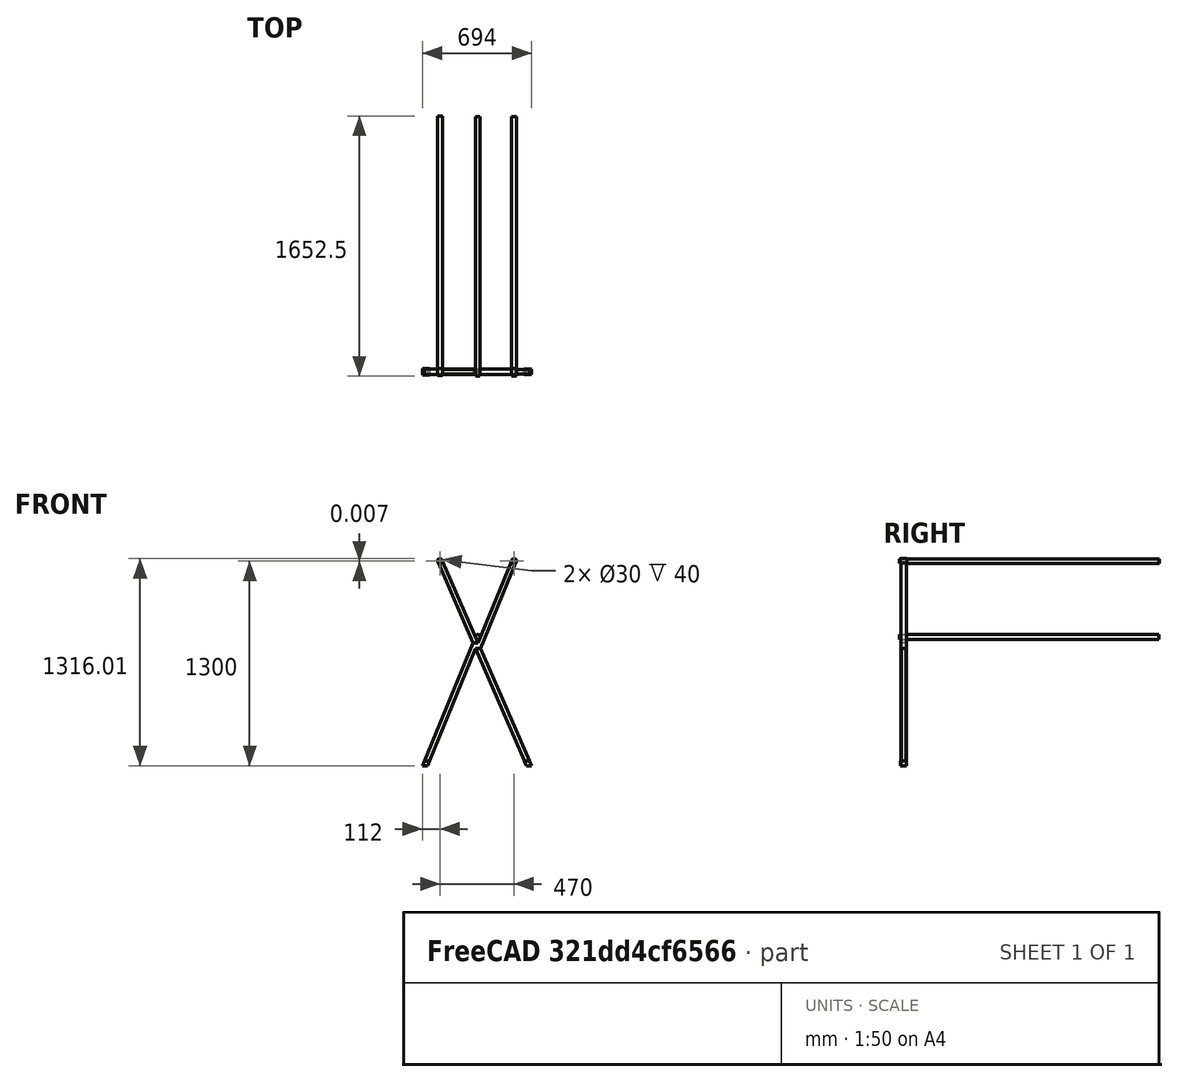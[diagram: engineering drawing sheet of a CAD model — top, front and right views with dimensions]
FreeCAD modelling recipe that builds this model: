
FCSTD DOCUMENT  (FreeCAD 1.0R39109 (Git))
Label: clothesdryingpole
License: All rights reserved
LicenseURL: https://en.wikipedia.org/wiki/All_rights_reserved
objects: Sketcher::SketchObject×9, PartDesign::Pad×8, PartDesign::ShapeBinder×5, PartDesign::Body×4, PartDesign::Line×2, App::Part×2, PartDesign::Pocket×1, Part::FeaturePython×1, Assembly::JointGroup×1, App::Link×1, Assembly::AssemblyObject×1
note: 56 computed .brp shape members not serialized (recipe doc carries the construction recipe); baked Part::Feature solids carry a one-line shape summary decoded from their .brp

FEATURE [Sketcher::SketchObject] Sketch
  ArcFitTolerance = 1e-06
  AttachmentSupport = -> [XZ_Plane]
  FullyConstrained = true
  MakeInternals = false
  MapMode = 5
  Placement = pos=(0,0,0) rot=(1,0,0;1.5708rad)
  sketch-geometry (16):
    g0: LineSegment StartX=-345 StartY=0 StartZ=0 EndX=-315 EndY=0 EndZ=0
    g1: LineSegment [constr] StartX=315 StartY=0 StartZ=0 EndX=345 EndY=0 EndZ=0
    g2: LineSegment [constr] StartX=-250 StartY=1300 StartZ=0 EndX=-220 EndY=1300 EndZ=0
    g3: LineSegment StartX=220 StartY=1300 StartZ=0 EndX=250 EndY=1300 EndZ=0
    g4: LineSegment [constr] StartX=-220 StartY=1300 StartZ=0 EndX=345 EndY=0 EndZ=0
    g5: LineSegment [constr] StartX=315 StartY=0 StartZ=0 EndX=-250 EndY=1300 EndZ=0
    g6: LineSegment StartX=220 StartY=1300 StartZ=0 EndX=6 EndY=780 EndZ=0
    g7: LineSegment StartX=-345 StartY=0 StartZ=0 EndX=-24 EndY=780 EndZ=0
    g8: LineSegment StartX=-315 StartY=0 StartZ=0 EndX=-8.59091 EndY=744.545 EndZ=0
    g9: LineSegment StartX=250 StartY=1300 StartZ=0 EndX=21.4091 EndY=744.545 EndZ=0
    g10: LineSegment [constr] StartX=-8.59091 StartY=744.545 StartZ=0 EndX=-8.59091 EndY=780 EndZ=0
    g11: LineSegment [constr] StartX=-8.59091 StartY=780 StartZ=0 EndX=-24 EndY=780 EndZ=0
    g12: LineSegment [constr] StartX=6 StartY=780 StartZ=0 EndX=6 EndY=744.545 EndZ=0
    g13: LineSegment [constr] StartX=21.4091 StartY=744.545 StartZ=0 EndX=6 EndY=744.545 EndZ=0
    g14: LineSegment StartX=-24 StartY=780 StartZ=0 EndX=6 EndY=780 EndZ=0
    g15: LineSegment StartX=-8.59091 StartY=744.545 StartZ=0 EndX=21.4091 EndY=744.545 EndZ=0
  constraints (44):
    c: PointOnObject(g0,g-1)
    c: PointOnObject(g0,g-1)
    c: PointOnObject(g1,g-1)
    c: Symmetric(g1,g0,g-1)
    c: DistanceX(g0,g1) = 690
    c: Equal(g1,g0)
    c: Horizontal(g2)
    c: DistanceY(g-1,g2) = 1300
    c: Symmetric(g3,g2,g-2)
    c: Horizontal(g3)
    c: DistanceX(g2,g3) = 500
    c: Equal(g3,g2)
    c: Equal(g2,g1)
    c: Coincident(g4,g2)
    c: Coincident(g4,g1)
    c: Coincident(g5,g1)
    c: Coincident(g5,g2)
    c: Coincident(g6,g3)
    c: Coincident(g7,g0)
    c: Coincident(g8,g0)
    c: Parallel(g6,g8)
    c: Parallel(g8,g7)
    c: Coincident(g9,g3)
    c: Parallel(g9,g6)
    c: Coincident(g10,g8)
    c: Vertical(g10)
    c: Coincident(g11,g10)
    c: Coincident(g11,g7)
    c: Horizontal(g11)
    c: Coincident(g12,g6)
    c: Vertical(g12)
    c: Coincident(g13,g9)
    c: Coincident(g13,g12)
    c: Horizontal(g13)
    c: Equal(g13,g11)
    c: PointOnObject(g9,g4)
    c: PointOnObject(g7,g5)
    c: PointOnObject(g8,g5)
    c: Horizontal(g6,g7)
    c: DistanceX(g0,g0) = 30
    c: Coincident(g14,g7)
    c: Coincident(g14,g6)
    c: Coincident(g15,g8)
    c: Coincident(g15,g9)
FEATURE [PartDesign::Pad] Pad
  Direction = (0,-1,2e-16)
  Length = 35
  Length2 = 10
  Midplane = true
  Placement = pos=(0,0,0) rot=(1,0,0;1.5708rad)
  Profile = -> Sketch
  ReferenceAxis = -> Sketch [N_Axis]
  Refine = true
  Suppressed = false
  Type = 0
FEATURE [Sketcher::SketchObject] Sketch001
  ArcFitTolerance = 1e-06
  AttachmentSupport = -> [XZ_Plane]
  FullyConstrained = false
  MakeInternals = false
  MapMode = 5
  Placement = pos=(0,0,0) rot=(1,0,0;1.5708rad)
  sketch-geometry (4):
    g0: LineSegment StartX=315 StartY=0 StartZ=0 EndX=345 EndY=0 EndZ=0
    g1: LineSegment StartX=-250 StartY=1300 StartZ=0 EndX=-220 EndY=1300 EndZ=0
    g2: LineSegment StartX=-220 StartY=1300 StartZ=0 EndX=345 EndY=0 EndZ=0
    g3: LineSegment StartX=315 StartY=0 StartZ=0 EndX=-250 EndY=1300 EndZ=0
  constraints (9):
    c: PointOnObject(g0,g-1)
    c: Horizontal(g1)
    c: DistanceY(g-1,g1) = 1300
    c: Equal(g1,g0)
    c: Coincident(g2,g1)
    c: Coincident(g2,g0)
    c: Coincident(g3,g0)
    c: Coincident(g3,g1)
    c: DistanceX(g1,g1) = 30
FEATURE [PartDesign::Pad] Pad001
  BaseFeature = -> Pad
  Direction = (0,-1,2e-16)
  Length = 30
  Length2 = 10
  Midplane = true
  Placement = pos=(0,0,0) rot=(1,0,0;1.5708rad)
  Profile = -> Sketch001
  ReferenceAxis = -> Sketch001 [N_Axis]
  Refine = true
  Suppressed = false
  Type = 0
FEATURE [Sketcher::SketchObject] Sketch002
  ArcFitTolerance = 1e-06
  AttachmentSupport = -> [Pad001]
  ExternalGeometry = -> [Pad001]
  FullyConstrained = true
  MakeInternals = false
  MapMode = 5
  Placement = pos=(0,0,-1e-16) rot=(1,0,0;3.14159rad)
  sketch-geometry (8):
    g0: LineSegment StartX=-347 StartY=19.5 StartZ=0 EndX=-347 EndY=-19.5 EndZ=0
    g1: LineSegment StartX=-347 StartY=-19.5 StartZ=0 EndX=-313 EndY=-19.5 EndZ=0
    g2: LineSegment StartX=-313 StartY=-19.5 StartZ=0 EndX=-313 EndY=19.5 EndZ=0
    g3: LineSegment StartX=-313 StartY=19.5 StartZ=0 EndX=-347 EndY=19.5 EndZ=0
    g4: LineSegment [constr] StartX=-345 StartY=17.5 StartZ=0 EndX=-347 EndY=17.5 EndZ=0
    g5: LineSegment [constr] StartX=-345 StartY=17.5 StartZ=0 EndX=-345 EndY=19.5 EndZ=0
    g6: LineSegment [constr] StartX=-315 StartY=-17.5 StartZ=0 EndX=-315 EndY=-19.5 EndZ=0
    g7: LineSegment [constr] StartX=-315 StartY=-17.5 StartZ=0 EndX=-313 EndY=-17.5 EndZ=0
  constraints (24):
    c: Coincident(g0,g1)
    c: Coincident(g1,g2)
    c: Coincident(g2,g3)
    c: Coincident(g3,g0)
    c: Vertical(g0)
    c: Vertical(g2)
    c: Horizontal(g1)
    c: Horizontal(g3)
    c: Coincident(g4,g-3)
    c: PointOnObject(g4,g0)
    c: Horizontal(g4)
    c: Coincident(g5,g4)
    c: PointOnObject(g5,g3)
    c: Vertical(g5)
    c: Coincident(g6,g-4)
    c: PointOnObject(g6,g1)
    c: Vertical(g6)
    c: Coincident(g7,g6)
    c: PointOnObject(g7,g2)
    c: Horizontal(g7)
    c: Equal(g7,g6)
    c: Equal(g6,g5)
    c: Equal(g5,g4)
    c: DistanceY(g5,g5) = 2
FEATURE [PartDesign::Pad] Pad002
  BaseFeature = -> Pad001
  Direction = (0.380571,2e-16,0.924752)
  Length = 30
  Length2 = 10
  Placement = pos=(0,0,0) rot=(1,0,0;1.5708rad)
  Profile = -> Sketch002
  ReferenceAxis = -> Pad001 [Edge24]
  Refine = true
  Suppressed = false
  Type = 0
FEATURE [Sketcher::SketchObject] Sketch003
  ArcFitTolerance = 1e-06
  AttachmentSupport = -> [Pad002]
  ExternalGeometry = -> [Pad002]
  FullyConstrained = true
  MakeInternals = false
  MapMode = 5
  Placement = pos=(0,0,-1e-16) rot=(1,0,0;3.14159rad)
  sketch-geometry (8):
    g0: LineSegment StartX=313 StartY=17 StartZ=0 EndX=313 EndY=-17 EndZ=0
    g1: LineSegment StartX=313 StartY=-17 StartZ=0 EndX=347 EndY=-17 EndZ=0
    g2: LineSegment StartX=347 StartY=-17 StartZ=0 EndX=347 EndY=17 EndZ=0
    g3: LineSegment StartX=347 StartY=17 StartZ=0 EndX=313 EndY=17 EndZ=0
    g4: LineSegment [constr] StartX=315 StartY=15 StartZ=0 EndX=313 EndY=15 EndZ=0
    g5: LineSegment [constr] StartX=315 StartY=15 StartZ=0 EndX=315 EndY=17 EndZ=0
    g6: LineSegment [constr] StartX=345 StartY=-15 StartZ=0 EndX=345 EndY=-17 EndZ=0
    g7: LineSegment [constr] StartX=345 StartY=-15 StartZ=0 EndX=347 EndY=-15 EndZ=0
  constraints (24):
    c: Coincident(g0,g1)
    c: Coincident(g1,g2)
    c: Coincident(g2,g3)
    c: Coincident(g3,g0)
    c: Vertical(g0)
    c: Vertical(g2)
    c: Horizontal(g1)
    c: Horizontal(g3)
    c: Coincident(g4,g-3)
    c: PointOnObject(g4,g0)
    c: Horizontal(g4)
    c: Coincident(g5,g4)
    c: PointOnObject(g5,g3)
    c: Vertical(g5)
    c: Coincident(g6,g-4)
    c: PointOnObject(g6,g1)
    c: Vertical(g6)
    c: Coincident(g7,g6)
    c: PointOnObject(g7,g2)
    c: Horizontal(g7)
    c: Equal(g5,g4)
    c: Equal(g4,g6)
    c: Equal(g6,g7)
    c: DistanceY(g5,g5) = 2
FEATURE [PartDesign::Pad] Pad003
  BaseFeature = -> Pad002
  Direction = (-0.398597,2e-16,0.917126)
  Length = 30
  Length2 = 10
  Placement = pos=(0,0,0) rot=(1,0,0;1.5708rad)
  Profile = -> Sketch003
  ReferenceAxis = -> Pad002 [Edge49]
  Refine = true
  Suppressed = false
  Type = 0
FEATURE [Sketcher::SketchObject] Sketch004
  ArcFitTolerance = 1e-06
  AttachmentSupport = -> [XZ_Plane]
  ExternalGeometry = -> [Pad003]
  FullyConstrained = true
  MakeInternals = false
  MapMode = 5
  Placement = pos=(0,0,0) rot=(1,0,0;1.5708rad)
  sketch-geometry (4):
    g0: Circle CenterX=-235 CenterY=1300 CenterZ=0 NormalX=0 NormalY=0 NormalZ=1 AngleXU=0 Radius=15
    g1: LineSegment [constr] StartX=-220 StartY=1300 StartZ=0 EndX=-219 EndY=1300 EndZ=0
    g2: Circle CenterX=235 CenterY=1300 CenterZ=0 NormalX=0 NormalY=0 NormalZ=1 AngleXU=0 Radius=15
    g3: LineSegment [constr] StartX=220 StartY=1300 StartZ=0 EndX=219 EndY=1300 EndZ=0
  constraints (14):
    c: PointOnObject(g1,g0)
    c: Horizontal(g1)
    c: DistanceX(g1,g1) = 1
    c: PointOnObject(g-3,g0)
    c: PointOnObject(g-3,g0)
    c: Horizontal(g1,g0)
    c: PointOnObject(g3,g2)
    c: Horizontal(g3,g2)
    c: Horizontal(g3)
    c: Radius(g0) = 15
    c: DistanceX(g3,g3) = 1
    c: Radius(g2) = 15
    c: PointOnObject(g-4,g2)
    c: PointOnObject(g-4,g2)
FEATURE [PartDesign::Pocket] Pocket
  BaseFeature = -> Pad003
  Direction = (0,1,-2e-16)
  Length = 40
  Length2 = 5
  Midplane = true
  Placement = pos=(0,0,0) rot=(1,0,0;1.5708rad)
  Profile = -> Sketch004
  ReferenceAxis = -> Sketch004 [N_Axis]
  Refine = true
  Suppressed = false
  Type = 0
FEATURE [Sketcher::SketchObject] Sketch005
  ArcFitTolerance = 1e-06
  AttachmentSupport = -> [XZ_Plane]
  ExternalGeometry = -> [Pocket]
  FullyConstrained = false
  MakeInternals = false
  MapMode = 5
  Placement = pos=(0,0,0) rot=(1,0,0;1.5708rad)
  sketch-geometry (6):
    g0: Circle CenterX=-235 CenterY=1300.01 CenterZ=0 NormalX=0 NormalY=0 NormalZ=1 AngleXU=0 Radius=15
    g1: Circle CenterX=-235 CenterY=1300.01 CenterZ=0 NormalX=0 NormalY=0 NormalZ=1 AngleXU=0 Radius=16
    g2: Circle CenterX=235 CenterY=1300 CenterZ=0 NormalX=0 NormalY=0 NormalZ=1 AngleXU=0 Radius=16
    g3: LineSegment [constr] StartX=220 StartY=1300 StartZ=0 EndX=219 EndY=1300 EndZ=0
    g4: LineSegment [constr] StartX=-220 StartY=1300 StartZ=0 EndX=-219 EndY=1300 EndZ=0
    g5: Circle CenterX=235 CenterY=1300 CenterZ=0 NormalX=0 NormalY=0 NormalZ=1 AngleXU=0 Radius=15
  constraints (13):
    c: Radius(g0) = 15
    c: Coincident(g1,g0)
    c: PointOnObject(g3,g2)
    c: PointOnObject(g4,g0)
    c: PointOnObject(g4,g1)
    c: Coincident(g4,g-4)
    c: Horizontal(g4)
    c: Coincident(g3,g-3)
    c: Horizontal(g3)
    c: Equal(g4,g3)
    c: DistanceX(g4,g4) = 1
    c: Coincident(g5,g2)
    c: Radius(g5) = 15
FEATURE [PartDesign::Pad] Pad004
  BaseFeature = -> Pocket
  Direction = (0,-1,2e-16)
  Length = 40
  Length2 = 10
  Midplane = true
  Placement = pos=(0,0,0) rot=(1,0,0;1.5708rad)
  Profile = -> Sketch005
  ReferenceAxis = -> Sketch005 [N_Axis]
  Refine = true
  Suppressed = false
  Type = 0
FEATURE [PartDesign::Body] Body
  AllowCompound = false
  Group = -> [Sketch,Pad,Sketch001,Pad001,Sketch002,Pad002,Sketch003,Pad003,Sketch004,Pocket,Sketch005,Pad004]
  Origin = -> Origin
  Tip = -> Pad004
FEATURE [Part::FeaturePython] Array  # Draft array (typed FeaturePython)
  AlwaysSyncPlacement = false
  Angle = 360
  ArrayType = 0
  Axis = (0,0,1)
  Base = -> Pad004
  Center = (0,0,0)
  Count = 2
  ExpandArray = false
  Fuse = false
  IntervalAxis = (0,0,0)
  IntervalX = (100,0,0)
  IntervalY = (0,1600,0)
  IntervalZ = (0,0,100)
  NumberCircles = 3
  NumberPolar = 5
  NumberX = 1
  NumberY = 2
  NumberZ = 1
  PlacementList = 2 placements: [(0,0,0),(0,1600,0)]
  RadialDistance = 50
  ScaleList = (2) [(1,1,1),(1,1,1)]
  Symmetry = 1
  TangentialDistance = 25
FEATURE [PartDesign::ShapeBinder] CopyPad004
  Placement = pos=(0,0,0) rot=(1,0,0;1.5708rad)
  TraceSupport = false
FEATURE [Sketcher::SketchObject] Sketch006
  ArcFitTolerance = 1e-06
  AttachmentSupport = -> [CopyPad004]
  FullyConstrained = false
  MakeInternals = false
  MapMode = 5
  Placement = pos=(0,-17.5,3.8e-15) rot=(1,0,0;1.5708rad)
  sketch-geometry (2):
    g0: Circle CenterX=-235 CenterY=1300.01 CenterZ=0 NormalX=0 NormalY=0 NormalZ=1 AngleXU=0 Radius=15
    g1: Circle CenterX=235 CenterY=1300 CenterZ=0 NormalX=0 NormalY=0 NormalZ=1 AngleXU=0 Radius=15
  constraints (2):
    c: Radius(g0) = 15
    c: Radius(g1) = 15
FEATURE [PartDesign::Pad] Pad005
  Direction = (0,-1,2e-16)
  Length = 1650
  Length2 = 10
  Placement = pos=(0,0,0) rot=(1,0,0;1.5708rad)
  Profile = -> Sketch006
  ReferenceAxis = -> Sketch006 [N_Axis]
  Refine = true
  Suppressed = false
  Type = 0
FEATURE [PartDesign::Body] Body001
  AllowCompound = false
  Group = -> [CopyPad004,Sketch006,Pad005]
  Origin = -> Origin001
  Placement = pos=(0,1640,0) rot=(0,0,1;0rad)
  Tip = -> Pad005
FEATURE [PartDesign::ShapeBinder] CopyPad005
  Placement = pos=(0,0,0) rot=(1,0,0;1.5708rad)
  TraceSupport = false
FEATURE [Sketcher::SketchObject] Sketch007
  ArcFitTolerance = 1e-06
  AttachmentSupport = -> [CopyPad005]
  FullyConstrained = false
  MakeInternals = false
  MapMode = 5
  Placement = pos=(0,-15,3.3e-15) rot=(1,0,0;1.5708rad)
  sketch-geometry (1):
    g0: Circle CenterX=-235 CenterY=1300.01 CenterZ=0 NormalX=0 NormalY=0 NormalZ=1 AngleXU=0 Radius=15
  constraints (1):
    c: Radius(g0) = 15
FEATURE [PartDesign::Pad] Pad006
  Direction = (0,-1,2e-16)
  Length = 1650
  Length2 = 10
  Placement = pos=(0,0,0) rot=(1,0,0;1.5708rad)
  Profile = -> Sketch007
  ReferenceAxis = -> Sketch007 [N_Axis]
  Refine = true
  Suppressed = false
  Type = 0
FEATURE [PartDesign::Body] Body002
  AllowCompound = false
  Group = -> [CopyPad005,Sketch007,Pad006]
  Origin = -> Origin002
  Placement = pos=(0,1640,0) rot=(0,0,1;0rad)
  Tip = -> Pad006
FEATURE [PartDesign::ShapeBinder] CopyPad006
  Placement = pos=(0,-15,3.3e-15) rot=(1,0,0;1.5708rad)
  TraceSupport = false
FEATURE [PartDesign::Line] DatumLine
  AttacherType = Attacher::AttachEngineLine
  AttachmentSupport = -> [CopyPad006]
  Length = 20
  MapMode = 29
  Placement = pos=(290.187,-15,126.12) rot=(0.699587,0.699587,0.145454;2.85271rad)
  ResizeMode = 0
FEATURE [PartDesign::ShapeBinder] CopyPad007
  Placement = pos=(0,-17.5,3.9e-15) rot=(1,0,0;1.5708rad)
  TraceSupport = false
FEATURE [PartDesign::Line] DatumLine001
  AttacherType = Attacher::AttachEngineLine
  AttachmentSupport = -> [CopyPad007]
  Length = 20
  MapMode = 29
  Placement = pos=(-269.377,-17.5,110.859) rot=(0.700295,-0.700295,-0.138466;2.86641rad)
  ResizeMode = 0
FEATURE [PartDesign::ShapeBinder] CopyPad008
  Placement = pos=(0,0,0) rot=(1,0,0;1.5708rad)
  TraceSupport = false
FEATURE [Sketcher::SketchObject] Sketch008
  ArcFitTolerance = 1e-06
  AttachmentSupport = -> [CopyPad008]
  ExternalGeometry = -> [DatumLine,DatumLine001]
  FullyConstrained = true
  MakeInternals = false
  MapMode = 5
  Placement = pos=(0,-17.5,3.8e-15) rot=(1,0,0;1.5708rad)
  sketch-geometry (1):
    g0: Circle CenterX=5.62322 CenterY=818.499 CenterZ=0 NormalX=0 NormalY=0 NormalZ=1 AngleXU=0 Radius=15
  constraints (3):
    c: Radius(g0) = 15
    c: Tangent(g0,g-4)
    c: Tangent(g0,g-3)
FEATURE [PartDesign::Pad] Pad007
  Direction = (0,-1,2e-16)
  Length = 1650
  Length2 = 10
  Placement = pos=(0,0,0) rot=(1,0,0;1.5708rad)
  Profile = -> Sketch008
  ReferenceAxis = -> Sketch008 [N_Axis]
  Refine = true
  Suppressed = false
  Type = 0
FEATURE [PartDesign::Body] Body003
  AllowCompound = false
  Group = -> [DatumLine,CopyPad006,DatumLine001,CopyPad007,CopyPad008,Sketch008,Pad007]
  Origin = -> Origin003
  Placement = pos=(0,1640,0) rot=(0,0,1;0rad)
  Tip = -> Pad007
FEATURE [App::Part] Part
  Group = -> [Body,Array,Body001,Body002,Body003]
  Origin = -> Origin004
  Placement = pos=(0,-812.5,0) rot=(0,0,1;0rad)
FEATURE [Assembly::JointGroup] Joints
FEATURE [App::Link] Part001
  LinkedObject = -> Part
FEATURE [Assembly::AssemblyObject] Assembly
  Group = -> [Joints,Part001]
  Origin = -> Origin005
  Placement = pos=(0,-812.5,0) rot=(0,0,1;0rad)
  Type = Assembly
FEATURE [App::Part] Part002  label="clothesdryingpole"
  Group = -> [Assembly,Part]
  Origin = -> Origin006
